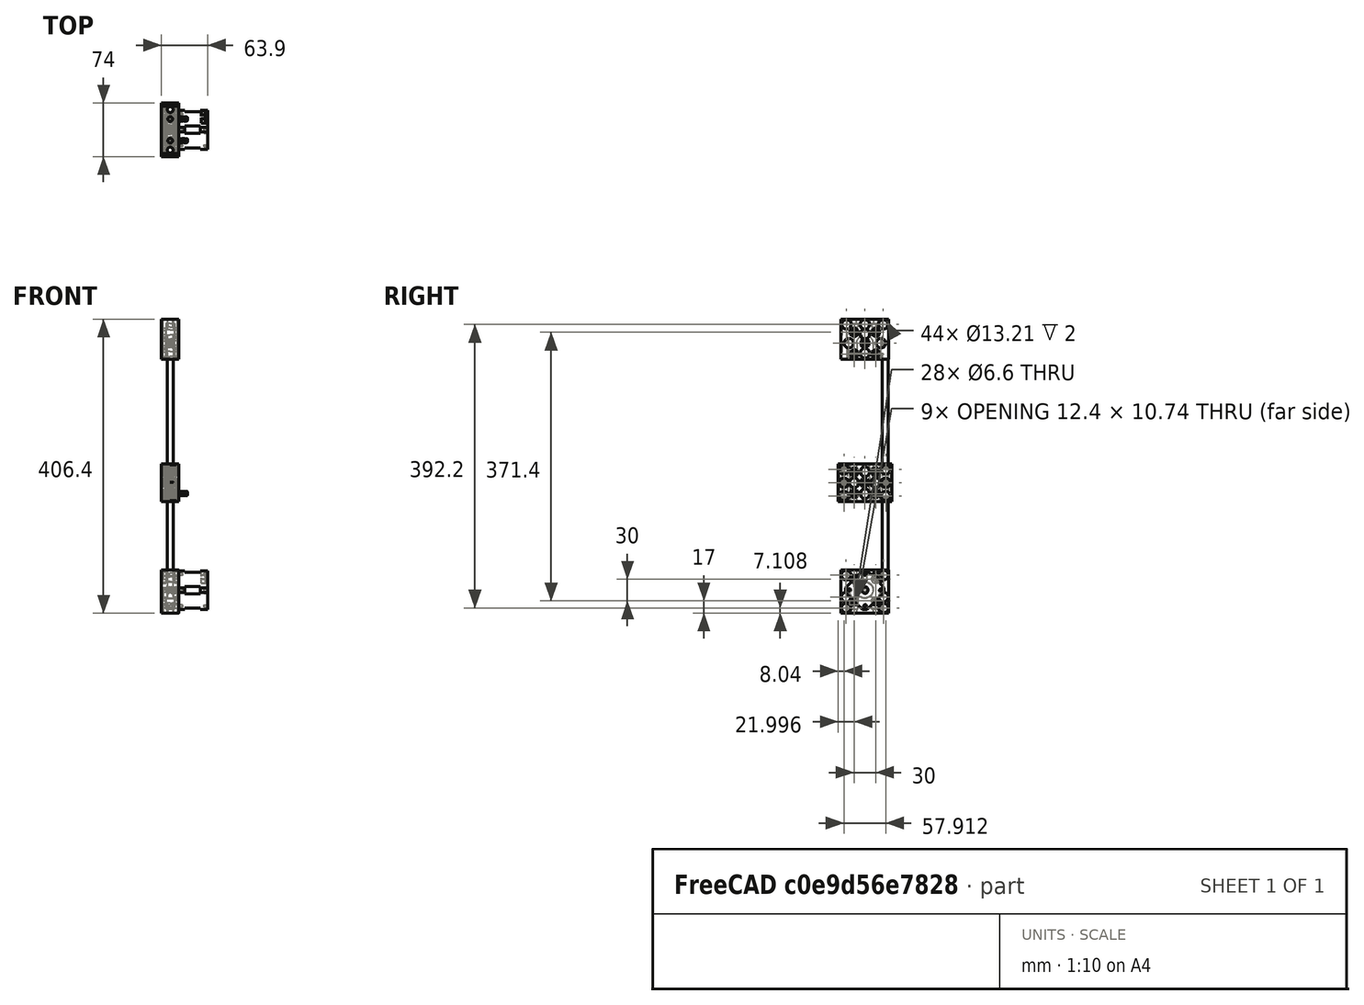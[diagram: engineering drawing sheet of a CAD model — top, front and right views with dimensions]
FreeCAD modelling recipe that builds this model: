
FCSTD DOCUMENT  (FreeCAD 0.16R6707 (Git))
Label: D3D Left Z Axis Simple
License: CreativeCommons Attribution
LicenseURL: http://creativecommons.org/licenses/by/4.0/
objects: Part::FeaturePython×7, Part::Feature×7, App::FeaturePython×4, Part::Mirroring×3, Part::MultiFuse×3, Part::Cylinder×1, App::DocumentObjectGroup×1
note: 21 computed .brp shape members not serialized (recipe doc carries the construction recipe); baked Part::Feature solids carry a one-line shape summary decoded from their .brp

FEATURE [Part::FeaturePython] Universal_axis_idler_side_01  # a2plus imported part (geometry in sourceFile) (typed FeaturePython)
  Placement = pos=(0,0,0) rot=(0.57735,0.57735,0.57735;2.0944rad)
  fixedPosition = true
  sourceFile = <userpath>/Downloads/Freecad/D3D Printer/Universal_axis_idler_side.fcstd
  timeLastImport = 1.48765e+09
  updateColors = true
FEATURE [Part::Mirroring] Part__Mirroring  label="Universal_axis_idler_side_01 (Mirror #1)"
  Base = (0,0,0)
  Normal = (1,0,0)
  Source = -> Universal_axis_idler_side_01
FEATURE [Part::MultiFuse] Fusion  label="Y1 Universal Axis Idler"
  Placement = pos=(12,32.9864,-33) rot=(-1,0,0;1.5708rad)
  Shapes = -> [Part__Mirroring,Universal_axis_idler_side_01]
FEATURE [Part::Cylinder] Cylinder  label="Rod"
  Angle = 360
  Height = 406.4
  Placement = pos=(12,4.98645,-1.61743e-05) rot=(0,1,0;3.14159rad)
  Radius = 3.96875
FEATURE [Part::FeaturePython] Clone006  label="Clone of Rod"  # Draft clone (typed FeaturePython)
  Objects = -> [Cylinder]
  Placement = pos=(11.9844,60.9864,-1.61743e-05) rot=(1,0,0;3.14159rad)
  Scale = (1,1,1)
FEATURE [Part::FeaturePython] Universal_axis_motor_side_01  # a2plus imported part (geometry in sourceFile) (typed FeaturePython)
  fixedPosition = false
  sourceFile = <userpath>/Downloads/Freecad/D3D Printer/Universal_axis_motor_side.fcstd
  timeLastImport = 1.48765e+09
  updateColors = true
FEATURE [Part::Mirroring] Part__Mirroring003  label="Universal_axis_motor_side_01 (Mirror #3)"
  Base = (0,0,0)
  Normal = (0,0,1)
  Source = -> Universal_axis_motor_side_01
FEATURE [Part::MultiFuse] Fusion005  label="Y1 Universal Axis Motor"
  Placement = pos=(12,32.9864,-374.4) rot=(0,-1,0;1.5708rad)
  Shapes = -> [Part__Mirroring003,Universal_axis_motor_side_01]
FEATURE [App::FeaturePython] planeConstraint01  label="Rods"  # a2plus constraint (typed FeaturePython)
  Object1 = Fusion005
  Object2 = Cylinder
  SubElement1 = Face3
  SubElement2 = Face2
  Type = plane
  directionConstraint = 0
  offset = 0
FEATURE [App::FeaturePython] planeConstraint02  label="Rods / Axis Motor "  # a2plus constraint (typed FeaturePython)
  Object1 = Fusion005
  Object2 = Clone006
  SubElement1 = Face42
  SubElement2 = Face2
  Type = plane
  directionConstraint = 0
  offset = 0
FEATURE [App::FeaturePython] planeConstraint03  label="Rods / Axis Idler"  # a2plus constraint (typed FeaturePython)
  Object1 = Fusion
  Object2 = Cylinder
  SubElement1 = Face3
  SubElement2 = Face3
  Type = plane
  directionConstraint = 1
  offset = 0
FEATURE [Part::FeaturePython] carriage_8mm_rods_01  # a2plus imported part (geometry in sourceFile) (typed FeaturePython)
  Placement = pos=(12.5,0,0) rot=(0,0,1;0rad)
  fixedPosition = false
  sourceFile = <userpath>/Downloads/Freecad/D3D Printer/Mess Stuff/axis_8mm STL + FCSTD/carriage_8mm_rods.FCStd
  timeLastImport = 1.48802e+09
  updateColors = true
FEATURE [Part::Mirroring] Part__Mirroring004  label="carriage_8mm_rods_01 (Mirror #3)"
  Base = (0,0,0)
  Normal = (0,0,1)
  Source = -> carriage_8mm_rods_01
FEATURE [Part::Feature] Part__Feature001  label="Pulley"
  Placement = pos=(20,32.9864,-374.4) rot=(0.357407,-0.357407,0.862856;1.71777rad)
  shape: bbox 11 x 12.62 x 12.62 mm, 94 faces (baked)
FEATURE [Part::Feature] Part__Feature002  label="MK8"
  Placement = pos=(16.9019,30.8149,-376.706) rot=(1,0,0;0.785398rad)
  shape: bbox 3 x 3.394 x 3.394 mm, 13 faces (baked)
FEATURE [App::DocumentObjectGroup] Group  label="nuts bolts"
FEATURE [Part::Feature] Part__Feature003  label="ball_bearing"
  Placement = pos=(14,32.9864,-33) rot=(-0.57735,-0.57735,0.57735;2.0944rad)
  shape: bbox 8 x 13.6 x 13.6 mm, 82 faces (baked)
FEATURE [Part::Feature] Part__Feature004  label="lmuu 8mm bearing"
  Placement = pos=(0,-28,0) rot=(0,0,1;1.5708rad)
  shape: bbox 24 x 15 x 15 mm, 38 faces (baked)
FEATURE [Part::FeaturePython] Clone  label="lmuu 8mm bearing001"  # Draft clone (typed FeaturePython)
  Objects = -> [Part__Feature004]
  Placement = pos=(25,-28,0) rot=(0,0,1;1.5708rad)
  Scale = (1,1,1)
FEATURE [Part::FeaturePython] Clone007  label="lmuu 8mm bearing002"  # Draft clone (typed FeaturePython)
  Objects = -> [Part__Feature004]
  Placement = pos=(0,28,0) rot=(0,0,1;1.5708rad)
  Scale = (1,1,1)
FEATURE [Part::FeaturePython] Clone008  label="lmuu 8mm bearing003"  # Draft clone (typed FeaturePython)
  Objects = -> [Clone007]
  Placement = pos=(25,28,0) rot=(0,0,1;1.5708rad)
  Scale = (1,1,1)
FEATURE [Part::MultiFuse] Fusion006  label="Y1 Universal Axis Carriage"
  Placement = pos=(11.9844,32.9864,-238.5) rot=(0,-1,0;1.5708rad)
  Shapes = -> [Part__Mirroring004,carriage_8mm_rods_01,Part__Feature004,Clone,Clone007,Clone008]
FEATURE [Part::Feature] Part__Feature007  label="M6x30 001"
  Placement = pos=(35.9844,17.9864,-241) rot=(0.57735,-0.57735,0.57735;4.18879rad)
  shape: bbox 36.21 x 10 x 10 mm, 148 faces (baked)
FEATURE [Part::Feature] Part__Feature  label="Nema 17 Step Motor"
  Placement = pos=(63.878,32.9864,-374.4) rot=(0.678598,0.281085,-0.678598;3.68962rad)
  shape: bbox 61.88 x 53.46 x 53.46 mm, 81 faces (baked)
FEATURE [App::FeaturePython] circularEdgeConstraint01  # a2plus constraint (typed FeaturePython)
  Object1 = Fusion005
  Object2 = Part__Feature
  SubElement1 = Edge21
  SubElement2 = Edge134
  Type = circularEdge
  directionConstraint = 0
  lockRotation = false
  offset = 0
FEATURE [Part::Feature] Part__Feature006  label="M6x30"
  Placement = pos=(35.9844,47.9121,-241.06) rot=(0.57735,-0.57735,0.57735;4.18879rad)
  shape: bbox 36.21 x 10 x 10 mm, 148 faces (baked)
